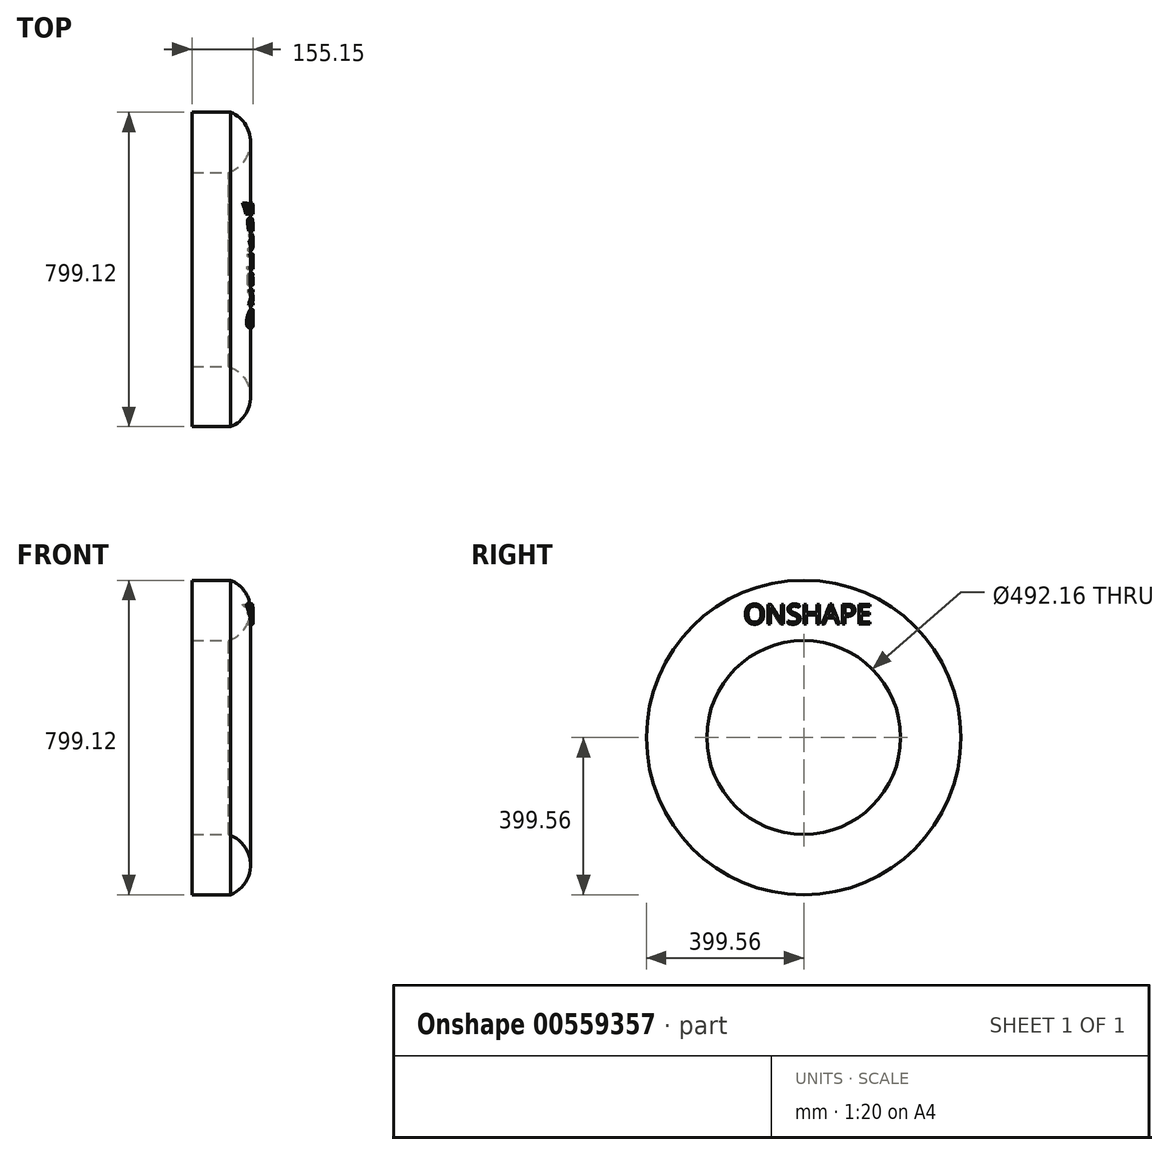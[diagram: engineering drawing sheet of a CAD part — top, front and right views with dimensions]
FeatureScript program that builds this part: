
annotation { "Feature Type Name" : "Feature", "Feature Type Description" : "" }
export const myFeature = defineFeature(function(context is Context, id is Id, definition is map)
    precondition{}
    {
        {
            var Q0;
            Q0=qCreatedBy(makeId("Front.planeOp"),FACE);
            var sketch = newSketch(context, id + "F0", { "sketchPlane" : qUnion([Q0])});
            skArc(sketch, "E0", {"start": v(0, 246.08) * mm, "mid": v(56.08, 320.69) * mm, "end": v(6.18, 399.56) * mm});
            skLineSegment(sketch, "E1", {"start": v(6.18, 399.56) * mm, "end": v(-92.65, 399.56) * mm});
            skLineSegment(sketch, "E2", {"start": v(-92.65, 399.56) * mm, "end": v(-92.65, 246.08) * mm});
            skLineSegment(sketch, "E3", {"start": v(-92.65, 246.08) * mm, "end": v(0, 246.08) * mm});
            skLineSegment(sketch, "E4", {"start": v(0, 0) * mm, "end": v(-188.73, 0) * mm, "construction": true});
            skSolve(sketch);
        }
        {
            var Q0;
            Q0=qSketchRegion(id+"F0",true);
            var Q1;
            Q1=sQuery(id+"F0.wireOp",EDGE,"E4");
            revolve(context, id + "F1", {"entities" : qUnion([Q0]), "axis" : qUnion([Q1]), "revolveType" : RevolveType.FULL});
        }
        {
            var Q0;
            Q0=qCreatedBy(makeId("Right.planeOp"),FACE);
            cPlane(context, id + "F2", {"entities" : qUnion([Q0]), "cplaneType" : CPlaneType.OFFSET, "offset" : 139.7 * mm, "width" : 152.4 * mm, "height" : 152.4 * mm});
        }
        {
            var Q0;
            Q0=qCreatedBy(id+"F2.planeOp",FACE);
            var sketch = newSketch(context, id + "F3", { "sketchPlane" : qUnion([Q0])});
            skText(sketch, "E5", { "text": "ONSHAPE", "fontName": "NotoSans-Regular.ttf"});
            const initialGuessF3  = {"E5": [-0.15235, 0.28834, 1, 0, 0.05057]};
            skSetInitialGuess(sketch, initialGuessF3);
            skSolve(sketch);
        }
        {
            var Q0;
            Q0=qSketchRegion(id+"F3",true);
            extrude(context, id + "F4", {"entities" : qUnion([Q0]), "operationType" : NewBodyOperationType.ADD, "endBound" : BoundingType.UP_TO_NEXT, "oppositeDirection" : true, "depth" : 25.4 * mm, "offsetDistance" : 25.4 * mm});
        }
        {
            var Q0;
            Q0=qCreatedBy(makeId("Front.planeOp"),FACE);
            var sketch = newSketch(context, id + "F5", { "sketchPlane" : qUnion([Q0])});
            skLineSegment(sketch, "E6", {"start": v(0, 0) * mm, "end": v(-188.73, 0) * mm, "construction": true});
            skArc(sketch, "E7.0", {"start": v(2, 240.06) * mm, "mid": v(62.42, 320.43) * mm, "end": v(8.67, 405.4) * mm});
            skLineSegment(sketch, "E8", {"start": v(8.67, 405.4) * mm, "end": v(25.37, 471.88) * mm});
            skLineSegment(sketch, "E9", {"start": v(25.37, 471.88) * mm, "end": v(161.26, 415.07) * mm});
            skLineSegment(sketch, "E10", {"start": v(161.26, 415.07) * mm, "end": v(172.6, 219.49) * mm});
            skLineSegment(sketch, "E11", {"start": v(172.6, 219.49) * mm, "end": v(2, 240.06) * mm});
            skSolve(sketch);
        }
        {
            var Q0;
            Q0=qSketchRegion(id+"F5",true);
            var Q1;
            Q1=sQuery(id+"F5.wireOp",EDGE,"E6");
            revolve(context, id + "F6", {"operationType" : NewBodyOperationType.REMOVE, "entities" : qUnion([Q0]), "axis" : qUnion([Q1]), "revolveType" : RevolveType.FULL, "oppositeDirection" : true});
        }
    });
